# Revit family: EDE-GRF-CCN_ Doccia Llave de Mesa para Cocina Cromo
name_source: partatom
category: Aparatos sanitarios
units: mm (PartAtom-declared; Revit-internal decimal feet)

## family parameters
Compartido = Sí
Corte con vacíos al cargar = No
Cota de conector redondo = Diámetro de uso
Número OmniClass = 23.45.00.00
Punto de cálculo de habitación = Sí
Se basa en plano de trabajo = No
Siempre vertical = Sí
Tipo de pieza = Normal
Título OmniClass = Sanitary, Laundry, and Cleaning Equipment

## types (1)
- DOCCIA LLAVE DE MESA PARA COCINA
    Conexión AC = Sí
    Conexión AF = Sí
    Conexión de residuos = Sí
    Conexión de ventilación = Sí
    Elevación por defecto = 0 m
    Fabricante = BRIGGS Ecuador
    Imagen de tipo = <Ninguno>
    Modelo = DOCCIA LLAVE DE MESA PARA COCINA
    URL = https://www.edesa.com.ec
    _ALT_Meson = 0.85 m
    _ALT_Toma = 0.55 m
    _EDESA_ Alto en cm = 30
    _EDESA_ Ancho en cm = 4
    _EDESA_ Categoría = Productos > Grifería > Cocina
    _EDESA_ Certificación = Cumple con norma NTE - INEN 3123 basada en la norma ASME 112.18.1 - 2012.
    _EDESA_ Color = Cromo
    _EDESA_ Conexión hidráulica = Entrada de agua: tubería ø 1/2" Salida de agua: tubería PVC 50
    _EDESA_ Consumo/capacidad de agua en L = 8.3 litros por minuto / 2.2 gpm a 60 psi
    _EDESA_ Descripción = Llave de cocina para agua fría. Instalación sobre fregadero o mesón. Incluye sifón.
    _EDESA_ Garantía = De por vida para el cuerpo principal y acabado en cromo (306)
    _EDESA_ Manual de instalación = https://www.edesa.com.ec
    _EDESA_ Marca = EDESA
    _EDESA_ Materiales = ABS cromado
    _EDESA_ Nombre = DOCCIA LLAVE DE MESA PARA COCINA
    _EDESA_ Productos incluídos = Sifón 1 1/2¨de Plástico
    _EDESA_ Productos necesarios para instalación = Desagüe 1 1/2", Llave Angular y Manguera Flexible
    _EDESA_ Profundidad en cm = 18
    _EDESA_ Sku/código = SG0070633061BO
    _EDESA_ Tipo de instalación = Sobre fregadero o mesón
